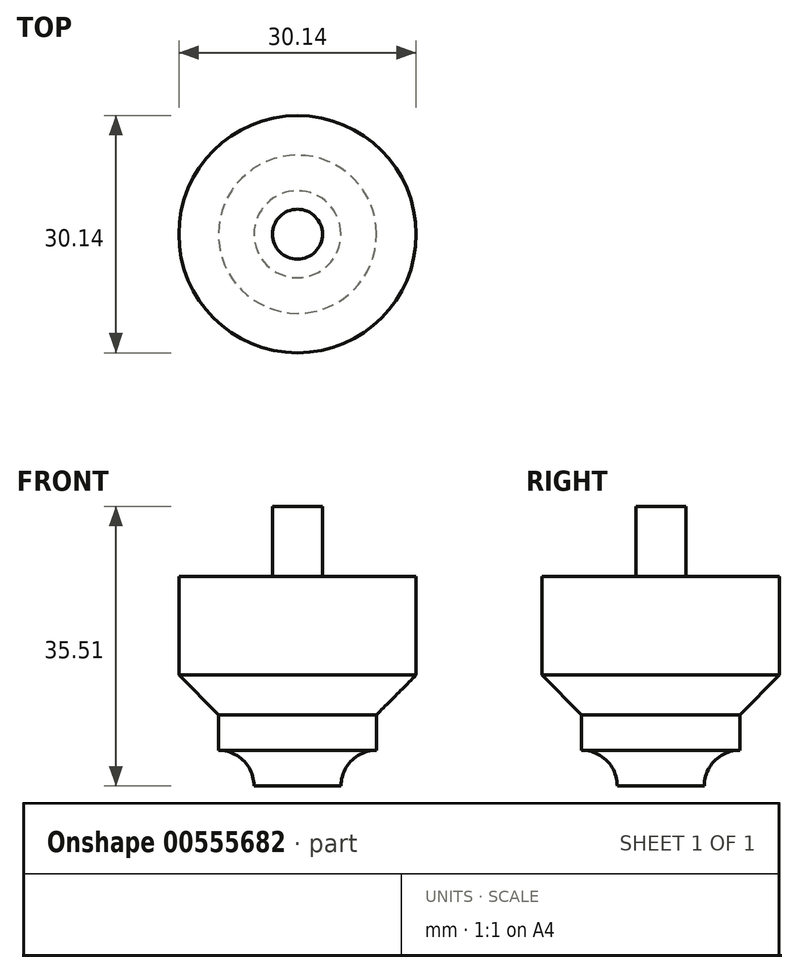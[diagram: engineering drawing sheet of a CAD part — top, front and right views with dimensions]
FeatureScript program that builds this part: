
annotation { "Feature Type Name" : "Feature", "Feature Type Description" : "" }
export const myFeature = defineFeature(function(context is Context, id is Id, definition is map)
    precondition{}
    {
        {
            var Q0;
            Q0=qCreatedBy(makeId("Front.planeOp"),FACE);
            var sketch = newSketch(context, id + "F0", { "sketchPlane" : qUnion([Q0])});
            skLineSegment(sketch, "E0", {"start": v(0, 26.62) * mm, "end": v(0, 14.07) * mm});
            skLineSegment(sketch, "E1", {"start": v(0, 14.07) * mm, "end": v(5.02, 9.04) * mm});
            skLineSegment(sketch, "E2", {"start": v(5.02, 9.04) * mm, "end": v(5.02, 4.52) * mm});
            skArc(sketch, "E3", {"start": v(9.54, 0) * mm, "mid": v(8.22, 3.2) * mm, "end": v(5.02, 4.52) * mm});
            skLineSegment(sketch, "E4", {"start": v(9.54, 0) * mm, "end": v(15.07, 0) * mm});
            skLineSegment(sketch, "E5", {"start": v(9.54, 0) * mm, "end": v(9.54, -5.17) * mm, "construction": true});
            skLineSegment(sketch, "E6.bottom", {"start": v(0, 26.62) * mm, "end": v(15.07, 26.62) * mm});
            skLineSegment(sketch, "E6.right", {"start": v(15.07, 26.62) * mm, "end": v(15.07, 0) * mm, "construction": true});
            skLineSegment(sketch, "E7.MirrorCS", {"start": v(30.14, 26.62) * mm, "end": v(30.14, 14.07) * mm});
            skLineSegment(sketch, "E8.MirrorCS", {"start": v(30.14, 14.07) * mm, "end": v(25.11, 9.04) * mm});
            skLineSegment(sketch, "E9.MirrorCS", {"start": v(25.11, 9.04) * mm, "end": v(25.11, 4.52) * mm});
            skArc(sketch, "E10.MirrorCS", {"start": v(20.6, 0) * mm, "mid": v(21.92, 3.2) * mm, "end": v(25.11, 4.52) * mm});
            skLineSegment(sketch, "E11", {"start": v(15.07, 0) * mm, "end": v(20.6, 0) * mm});
            skLineSegment(sketch, "E12", {"start": v(18.24, 26.62) * mm, "end": v(30.14, 26.62) * mm});
            skLineSegment(sketch, "E13.bottom", {"start": v(11.9, 35.5) * mm, "end": v(18.24, 35.5) * mm});
            skLineSegment(sketch, "E13.top", {"start": v(15.07, 26.62) * mm, "end": v(18.24, 26.62) * mm});
            skLineSegment(sketch, "E13.left", {"start": v(11.9, 35.5) * mm, "end": v(11.9, 26.62) * mm});
            skLineSegment(sketch, "E13.right", {"start": v(18.24, 35.5) * mm, "end": v(18.24, 26.62) * mm});
            skLineSegment(sketch, "E14", {"start": v(15.07, 35.5) * mm, "end": v(15.07, 26.62) * mm, "construction": true});
            skLineSegment(sketch, "E15", {"start": v(15.07, 35.5) * mm, "end": v(15.07, 0) * mm});
            skLineSegment(sketch, "E16", {"start": v(0, 14.07) * mm, "end": v(0, 0) * mm, "construction": true});
            skLineSegment(sketch, "E17", {"start": v(9.54, 0) * mm, "end": v(0, 0) * mm, "construction": true});
            skSolve(sketch);
        }
        {
            var Q0;
            Q0=makeQuery(id+"F0.imprint","IMPRINT",FACE,{"disambiguationData":[TD([[makeQuery(id+"F0.imprint","IMPRINT",EDGE,{"derivedFrom":sQuery(id+"F0.wireOp",EDGE,"E1")}),1.0]])]});
            var Q1;
            {var subQ3=sQuery(id+"F0.wireOp",EDGE,"E13.left");Q1=makeQuery(id+"F0.imprint","IMPRINT",FACE,{"disambiguationData":[TD([[makeQuery(id+"F0.imprint","IMPRINT",EDGE,{"derivedFrom":subQ3}),1.0]])]});}
            var Q2;
            Q2=sQuery(id+"F0.wireOp",EDGE,"E15");
            revolve(context, id + "F1", {"entities" : qUnion([Q0, Q1]), "axis" : qUnion([Q2]), "revolveType" : RevolveType.FULL});
        }
    });
